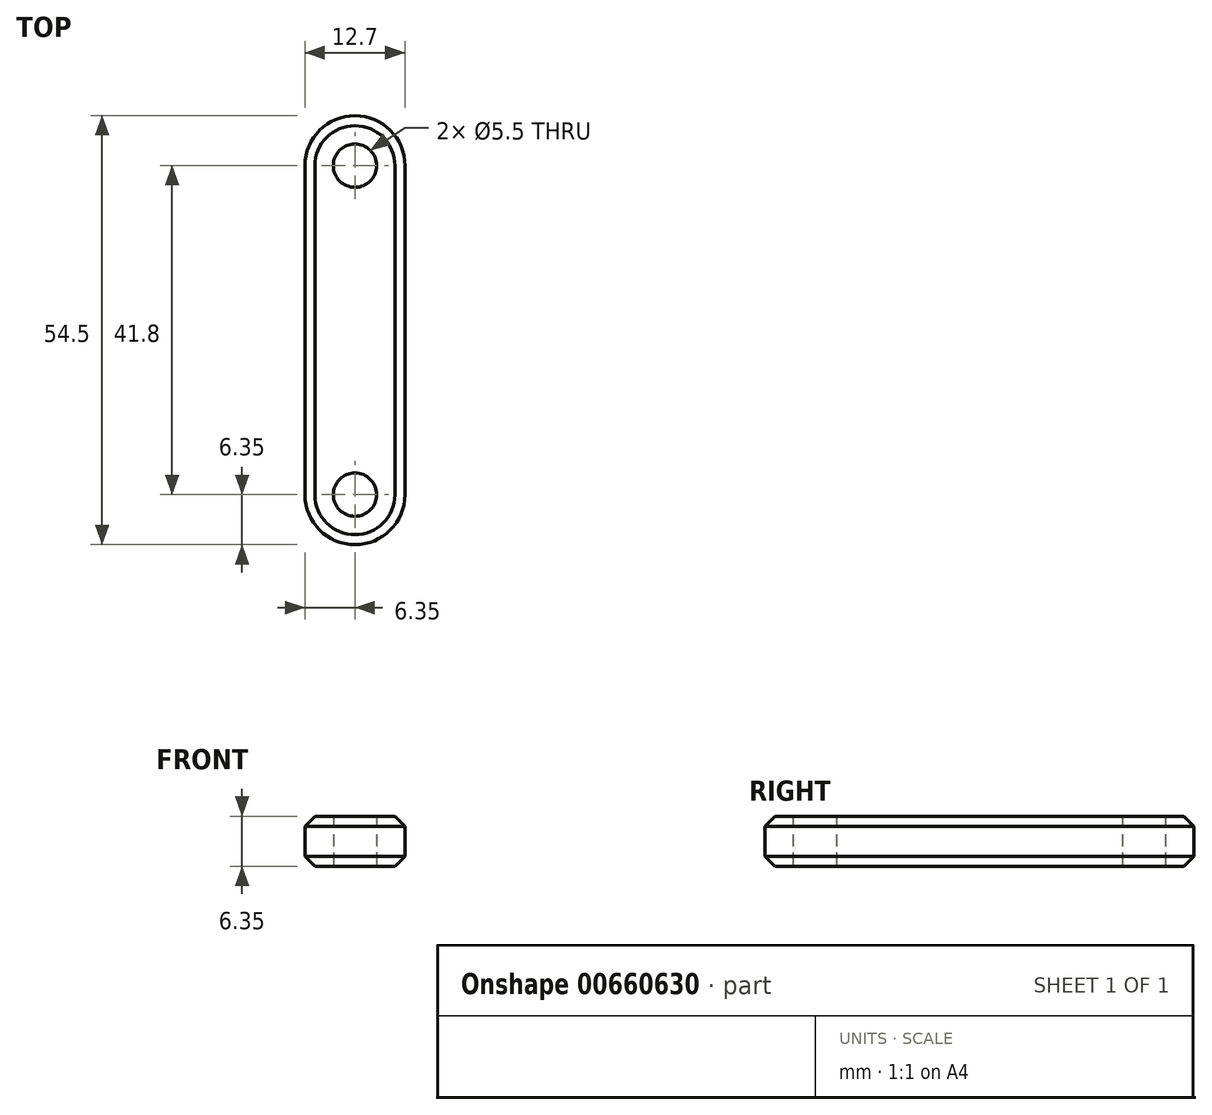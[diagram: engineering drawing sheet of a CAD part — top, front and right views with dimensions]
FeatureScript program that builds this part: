
annotation { "Feature Type Name" : "Feature", "Feature Type Description" : "" }
export const myFeature = defineFeature(function(context is Context, id is Id, definition is map)
    precondition{}
    {
        {
            var Q0;
            Q0=qCreatedBy(makeId("Top.planeOp"),FACE);
            var sketch = newSketch(context, id + "F0", { "sketchPlane" : qUnion([Q0])});
            skLineSegment(sketch, "E0.bottom", {"start": v(6.35, 27.25) * mm, "end": v(-6.35, 27.25) * mm});
            skLineSegment(sketch, "E0.top", {"start": v(6.35, -27.25) * mm, "end": v(-6.35, -27.25) * mm});
            skLineSegment(sketch, "E0.left", {"start": v(6.35, 27.25) * mm, "end": v(6.35, -27.25) * mm});
            skLineSegment(sketch, "E0.right", {"start": v(-6.35, 27.25) * mm, "end": v(-6.35, -27.25) * mm});
            skPoint(sketch, "E0.middle", {"position": v(0, 0) * mm});
            skLineSegment(sketch, "E1", {"start": v(0, 0) * mm, "end": v(0, -27.25) * mm});
            skLineSegment(sketch, "E2", {"start": v(0, -27.25) * mm, "end": v(0, -20.9) * mm});
            skCircle(sketch, "E3", {"center": v(0, -20.9) * mm, "radius": 6.35 * mm});
            skLineSegment(sketch, "E4", {"start": v(0, 27.25) * mm, "end": v(0, 20.9) * mm});
            skCircle(sketch, "E5", {"center": v(0, 20.9) * mm, "radius": 6.35 * mm});
            skLineSegment(sketch, "E6", {"start": v(0, -20.9) * mm, "end": v(2.75, -20.9) * mm});
            skCircle(sketch, "E7", {"center": v(0, -20.9) * mm, "radius": 2.75 * mm});
            skLineSegment(sketch, "E8", {"start": v(0, 20.9) * mm, "end": v(2.75, 20.9) * mm});
            skCircle(sketch, "E9", {"center": v(0, 20.9) * mm, "radius": 2.75 * mm});
            skSolve(sketch);
        }
        {
            var Q0;
            {var subQ0=sQuery(id+"F0.wireOp",EDGE,"E5");var subQ1=makeQuery(id+"F0.imprint","INTERSECT",VERTEX,{"derivedFrom":[sQuery(id+"F0.wireOp",EDGE,"E0.bottom"),subQ0]});Q0=makeQuery(id+"F0.imprint","IMPRINT",FACE,{"disambiguationData":[TD([[makeQuery(id+"F0.imprint","IMPRINT",EDGE,{"disambiguationData":[TD([[subQ1,1.0]])],"derivedFrom":subQ0}),1.0]])]});}
            var Q1;
            {var subQ1=sQuery(id+"F0.wireOp",EDGE,"E0.left");var subQ6=sQuery(id+"F0.wireOp",EDGE,"E5");var subQ8=makeQuery(id+"F0.imprint","INTERSECT",VERTEX,{"derivedFrom":[subQ1,subQ6]});Q1=makeQuery(id+"F0.imprint","IMPRINT",FACE,{"disambiguationData":[TD([[makeQuery(id+"F0.imprint","IMPRINT",EDGE,{"disambiguationData":[TD([[subQ8,-1.0]])],"derivedFrom":subQ1}),-1.0]])]});}
            var Q2;
            {var subQ0=sQuery(id+"F0.wireOp",EDGE,"E3");var subQ6=sQuery(id+"F0.wireOp",EDGE,"E1");var subQ7=makeQuery(id+"F0.imprint","INTERSECT",VERTEX,{"derivedFrom":[subQ6,subQ0]});Q2=makeQuery(id+"F0.imprint","IMPRINT",FACE,{"disambiguationData":[TD([[makeQuery(id+"F0.imprint","IMPRINT",EDGE,{"disambiguationData":[TD([[subQ7,-1.0]])],"derivedFrom":subQ6}),-1.0]])]});}
            var Q3;
            {var subQ0=sQuery(id+"F0.wireOp",EDGE,"E3");var subQ2=sQuery(id+"F0.wireOp",EDGE,"E1");var subQ3=makeQuery(id+"F0.imprint","INTERSECT",VERTEX,{"derivedFrom":[subQ2,subQ0]});Q3=makeQuery(id+"F0.imprint","IMPRINT",FACE,{"disambiguationData":[TD([[makeQuery(id+"F0.imprint","IMPRINT",EDGE,{"disambiguationData":[TD([[subQ3,-1.0]])],"derivedFrom":subQ2}),1.0]])]});}
            extrude(context, id + "F1", {"entities" : qUnion([Q0, Q1, Q2, Q3]), "depth" : 6.35 * mm, "offsetDistance" : 25.4 * mm});
        }
        {
            var Q0;
            Q0=makeQuery(id+"F1.opExtrude","CAP_EDGE",EDGE,{"disambiguationData":[OSD([sQuery(id+"F0.wireOp",EDGE,"E0.right")])],"isStart":true});
            var Q1;
            Q1=makeQuery(id+"F1.opExtrude","CAP_EDGE",EDGE,{"disambiguationData":[OSD([sQuery(id+"F0.wireOp",EDGE,"E0.right")])],"isStart":false});
            chamfer(context, id + "F2", {"entities" : qUnion([Q0, Q1]), "width" : 1.27 * mm, "tangentPropagation" : true});
        }
    });
